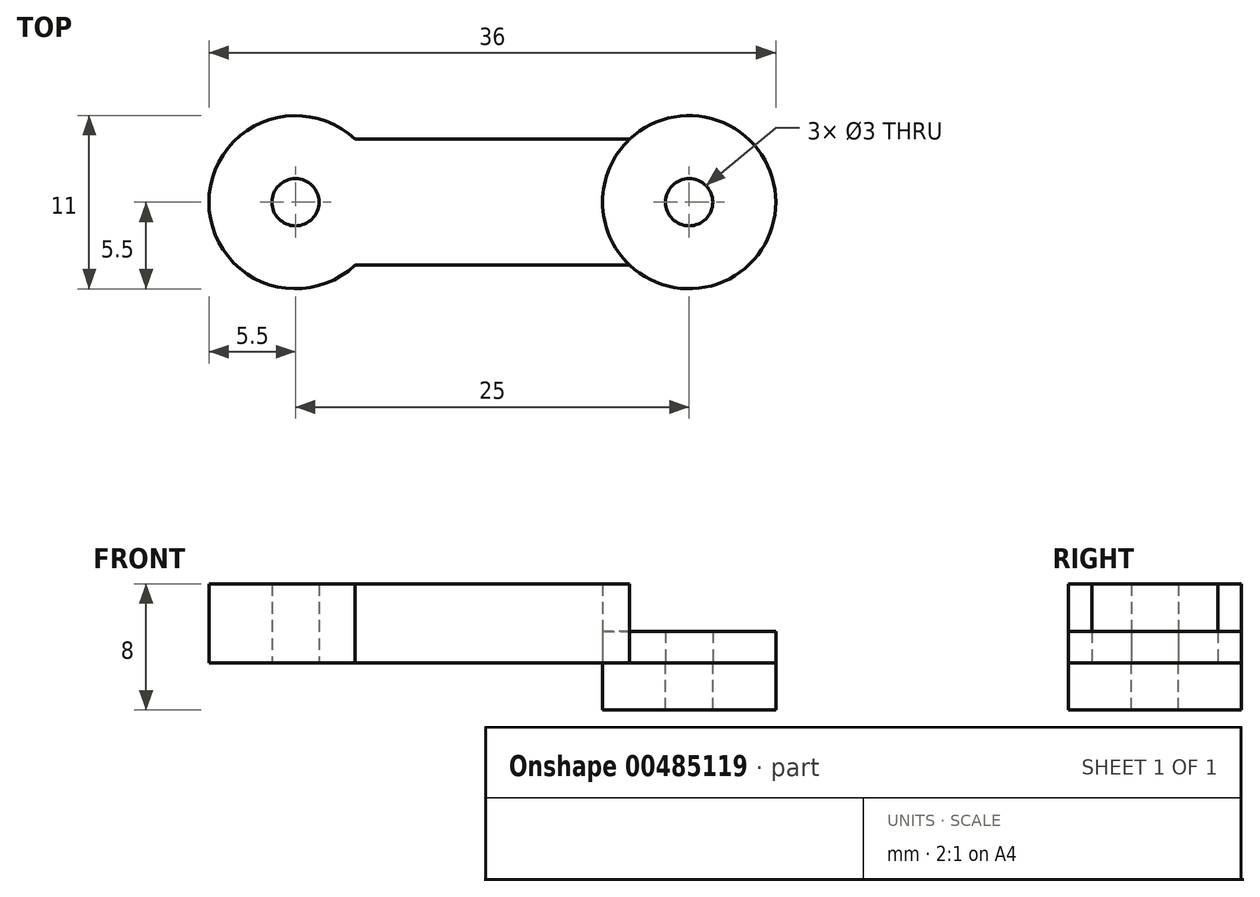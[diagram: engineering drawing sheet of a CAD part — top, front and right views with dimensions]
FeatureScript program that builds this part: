
annotation { "Feature Type Name" : "Feature", "Feature Type Description" : "" }
export const myFeature = defineFeature(function(context is Context, id is Id, definition is map)
    precondition{}
    {
        {
            var Q0;
            Q0=qCreatedBy(makeId("Top.planeOp"),FACE);
            var sketch = newSketch(context, id + "F0", { "sketchPlane" : qUnion([Q0])});
            skLineSegment(sketch, "E0.bottom", {"start": v(-37.32, 3.36) * mm, "end": v(-4.32, 3.36) * mm, "construction": true});
            skLineSegment(sketch, "E0.top", {"start": v(-37.32, -4.64) * mm, "end": v(-4.32, -4.64) * mm, "construction": true});
            skLineSegment(sketch, "E0.left", {"start": v(-37.32, 3.36) * mm, "end": v(-37.32, -4.64) * mm, "construction": true});
            skLineSegment(sketch, "E0.right", {"start": v(-4.32, 3.36) * mm, "end": v(-4.32, -4.64) * mm, "construction": true});
            skLineSegment(sketch, "E1", {"start": v(-29.32, 3.36) * mm, "end": v(-29.32, -4.64) * mm, "construction": true});
            skLineSegment(sketch, "E2", {"start": v(-12.32, -4.64) * mm, "end": v(-12.32, 3.36) * mm, "construction": true});
            skLineSegment(sketch, "E3", {"start": v(-37.32, -0.64) * mm, "end": v(-4.32, -0.64) * mm, "construction": true});
            skLineSegment(sketch, "E4", {"start": v(-33.32, 3.36) * mm, "end": v(-33.32, -4.64) * mm, "construction": true});
            skLineSegment(sketch, "E5", {"start": v(-8.32, 3.36) * mm, "end": v(-8.32, -4.64) * mm, "construction": true});
            skCircle(sketch, "E6", {"center": v(-33.32, -0.64) * mm, "radius": 5.5 * mm});
            skCircle(sketch, "E7", {"center": v(-8.32, -0.64) * mm, "radius": 5.5 * mm});
            skLineSegment(sketch, "E8", {"start": v(-29.32, 3.36) * mm, "end": v(-12.32, 3.36) * mm});
            skLineSegment(sketch, "E9", {"start": v(-29.32, -4.64) * mm, "end": v(-12.32, -4.64) * mm});
            skLineSegment(sketch, "E10", {"start": v(-12.32, 3.36) * mm, "end": v(-12.1, 3.36) * mm});
            skLineSegment(sketch, "E11", {"start": v(-12.32, -4.64) * mm, "end": v(-12.1, -4.64) * mm});
            skLineSegment(sketch, "E12", {"start": v(-29.32, -4.64) * mm, "end": v(-29.54, -4.64) * mm});
            skLineSegment(sketch, "E13", {"start": v(-29.32, 3.36) * mm, "end": v(-29.54, 3.36) * mm});
            skCircle(sketch, "E14", {"center": v(-33.32, -0.64) * mm, "radius": 1.5 * mm});
            skCircle(sketch, "E15", {"center": v(-8.32, -0.64) * mm, "radius": 1.5 * mm});
            skSolve(sketch);
        }
        {
            var Q0;
            Q0=makeQuery(id+"F0.imprint","IMPRINT",FACE,{"disambiguationData":[TD([[makeQuery(id+"F0.imprint","IMPRINT",EDGE,{"derivedFrom":sQuery(id+"F0.wireOp",EDGE,"E15")}),-1.0]])]});
            extrude(context, id + "F1", {"entities" : qUnion([Q0]), "oppositeDirection" : true, "depth" : 3 * mm, "offsetDistance" : 25 * mm});
        }
        {
            var Q0;
            Q0=makeQuery(id+"F0.imprint","IMPRINT",FACE,{"disambiguationData":[TD([[makeQuery(id+"F0.imprint","IMPRINT",EDGE,{"derivedFrom":sQuery(id+"F0.wireOp",EDGE,"E8")}),-1.0]])]});
            var Q1;
            Q1=makeQuery(id+"F0.imprint","IMPRINT",FACE,{"disambiguationData":[TD([[makeQuery(id+"F0.imprint","IMPRINT",EDGE,{"derivedFrom":sQuery(id+"F0.wireOp",EDGE,"E14")}),-1.0]])]});
            extrude(context, id + "F2", {"entities" : qUnion([Q0, Q1]), "depth" : 5 * mm, "offsetDistance" : 25 * mm});
        }
        {
            var Q0;
            Q0=makeQuery(id+"F1.opExtrude","CAP_FACE",FACE,{"disambiguationData":[OSD([sQuery(id+"F0.wireOp",EDGE,"E7"),sQuery(id+"F0.wireOp",EDGE,"E15")])],"isStart":true});
            extrude(context, id + "F3", {"entities" : qUnion([Q0]), "depth" : 2 * mm, "offsetDistance" : 25 * mm});
        }
    });
